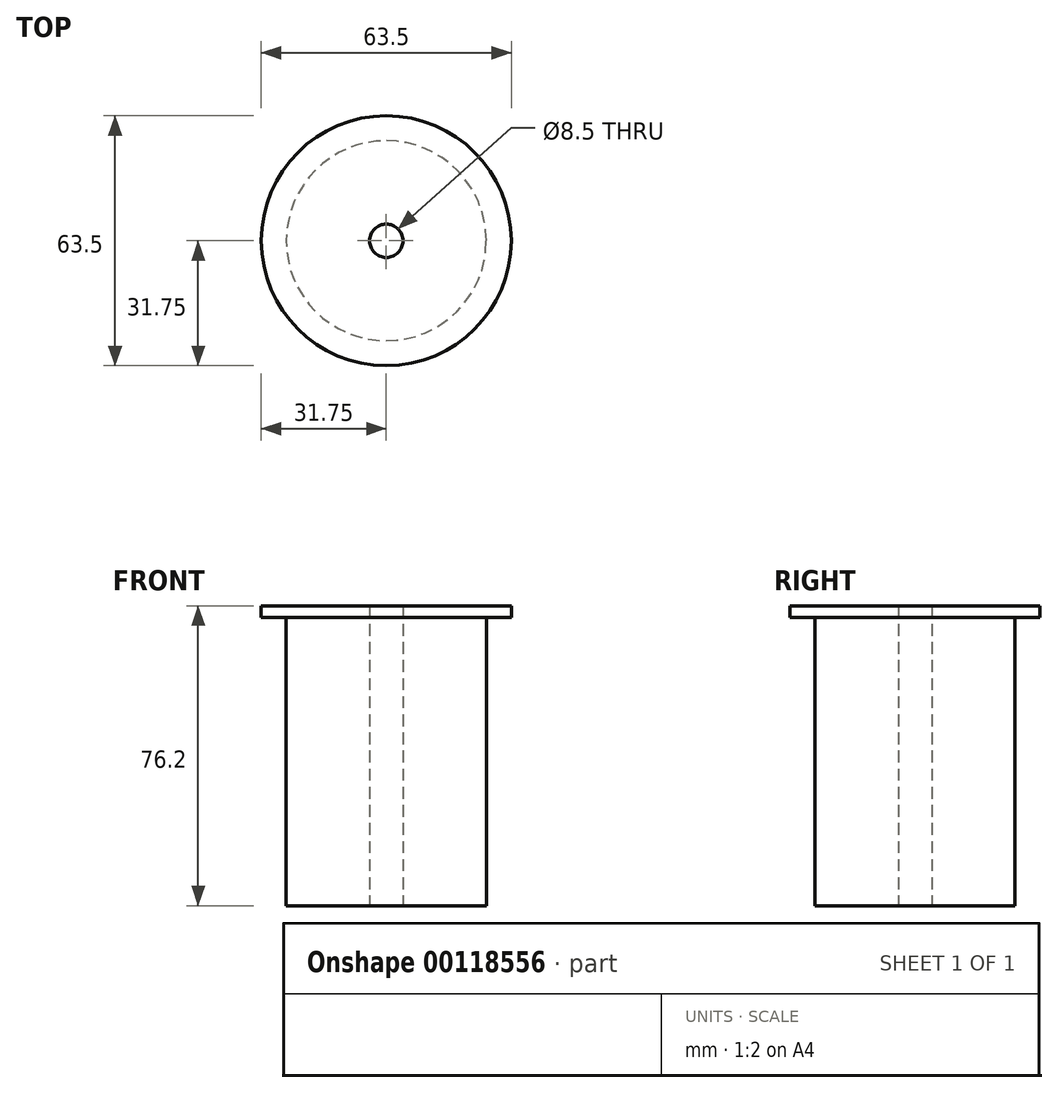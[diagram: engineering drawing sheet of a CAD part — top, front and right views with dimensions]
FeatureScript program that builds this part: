
annotation { "Feature Type Name" : "Feature", "Feature Type Description" : "" }
export const myFeature = defineFeature(function(context is Context, id is Id, definition is map)
    precondition{}
    {
        {
            var Q0;
            Q0=qCreatedBy(makeId("Top.planeOp"),FACE);
            var sketch = newSketch(context, id + "F0", { "sketchPlane" : qUnion([Q0])});
            skCircle(sketch, "E0", {"center": v(0, 0) * mm, "radius": 25.4 * mm});
            skCircle(sketch, "E1", {"center": v(0, 0) * mm, "radius": 4.25 * mm});
            skSolve(sketch);
        }
        {
            var Q0;
            Q0 = qSketchRegion(id + "F0", true);
            extrude(context, id + "F1", {"entities" : qUnion([Q0]), "depth" : 76.2 * mm});
        }
        {
            var Q0;
            Q0=makeQuery(id+"F1.opExtrude","CAP_FACE",FACE,{"disambiguationData":[OSD([sQuery(id+"F0.wireOp",EDGE,"E0"),sQuery(id+"F0.wireOp",EDGE,"E1")])],"isStart":true});
            var sketch = newSketch(context, id + "F2", { "sketchPlane" : qUnion([Q0])});
            skArc(sketch, "E2", {"start": v(-1.5, 22.35) * mm, "mid": v(-15.84, 15.84) * mm, "end": v(-22.35, 1.5) * mm});
            skLineSegment(sketch, "E3", {"start": v(-22.35, 1.5) * mm, "end": v(-7.1, 1.5) * mm});
            skLineSegment(sketch, "E4", {"start": v(-1.5, 22.35) * mm, "end": v(-1.5, 7.1) * mm});
            skArc(sketch, "E5", {"start": v(-1.5, 7.1) * mm, "mid": v(-5.13, 5.13) * mm, "end": v(-7.1, 1.5) * mm});
            skArc(sketch, "E6.MirrorCS", {"start": v(1.5, 7.1) * mm, "mid": v(5.13, 5.13) * mm, "end": v(7.1, 1.5) * mm});
            skLineSegment(sketch, "E7.MirrorCS", {"start": v(1.5, 22.35) * mm, "end": v(1.5, 7.1) * mm});
            skLineSegment(sketch, "E8.MirrorCS", {"start": v(22.35, 1.5) * mm, "end": v(7.1, 1.5) * mm});
            skArc(sketch, "E9.MirrorCS", {"start": v(1.5, 22.35) * mm, "mid": v(15.84, 15.84) * mm, "end": v(22.35, 1.5) * mm});
            skLineSegment(sketch, "E10.MirrorCS", {"start": v(-1.5, -22.35) * mm, "end": v(-1.5, -7.1) * mm});
            skArc(sketch, "E11.MirrorCS", {"start": v(-1.5, -7.1) * mm, "mid": v(-5.13, -5.13) * mm, "end": v(-7.1, -1.5) * mm});
            skArc(sketch, "E12.MirrorCS", {"start": v(1.5, -22.35) * mm, "mid": v(15.84, -15.84) * mm, "end": v(22.35, -1.5) * mm});
            skLineSegment(sketch, "E13.MirrorCS", {"start": v(-22.35, -1.5) * mm, "end": v(-7.1, -1.5) * mm});
            skLineSegment(sketch, "E14.MirrorCS", {"start": v(22.35, -1.5) * mm, "end": v(7.1, -1.5) * mm});
            skArc(sketch, "E15.MirrorCS", {"start": v(1.5, -7.1) * mm, "mid": v(5.13, -5.13) * mm, "end": v(7.1, -1.5) * mm});
            skArc(sketch, "E16.MirrorCS", {"start": v(-1.5, -22.35) * mm, "mid": v(-15.84, -15.84) * mm, "end": v(-22.35, -1.5) * mm});
            skLineSegment(sketch, "E17.MirrorCS", {"start": v(1.5, -22.35) * mm, "end": v(1.5, -7.1) * mm});
            skSolve(sketch);
        }
        {
            var Q0;
            Q0=makeQuery(id+"F1.opExtrude","CAP_FACE",FACE,{"disambiguationData":[OSD([sQuery(id+"F0.wireOp",EDGE,"E0"),sQuery(id+"F0.wireOp",EDGE,"E1")])],"isStart":false});
            var sketch = newSketch(context, id + "F3", { "sketchPlane" : qUnion([Q0])});
            skCircle(sketch, "E18", {"center": v(0, 0) * mm, "radius": 31.75 * mm});
            skCircle(sketch, "E19", {"center": v(0, 0) * mm, "radius": 25.4 * mm});
            skSolve(sketch);
        }
        {
            var Q0;
            Q0 = qSketchRegion(id + "F3", true);
            extrude(context, id + "F4", {"entities" : qUnion([Q0]), "operationType" : NewBodyOperationType.ADD, "oppositeDirection" : true, "depth" : 3 * mm});
        }
    });
